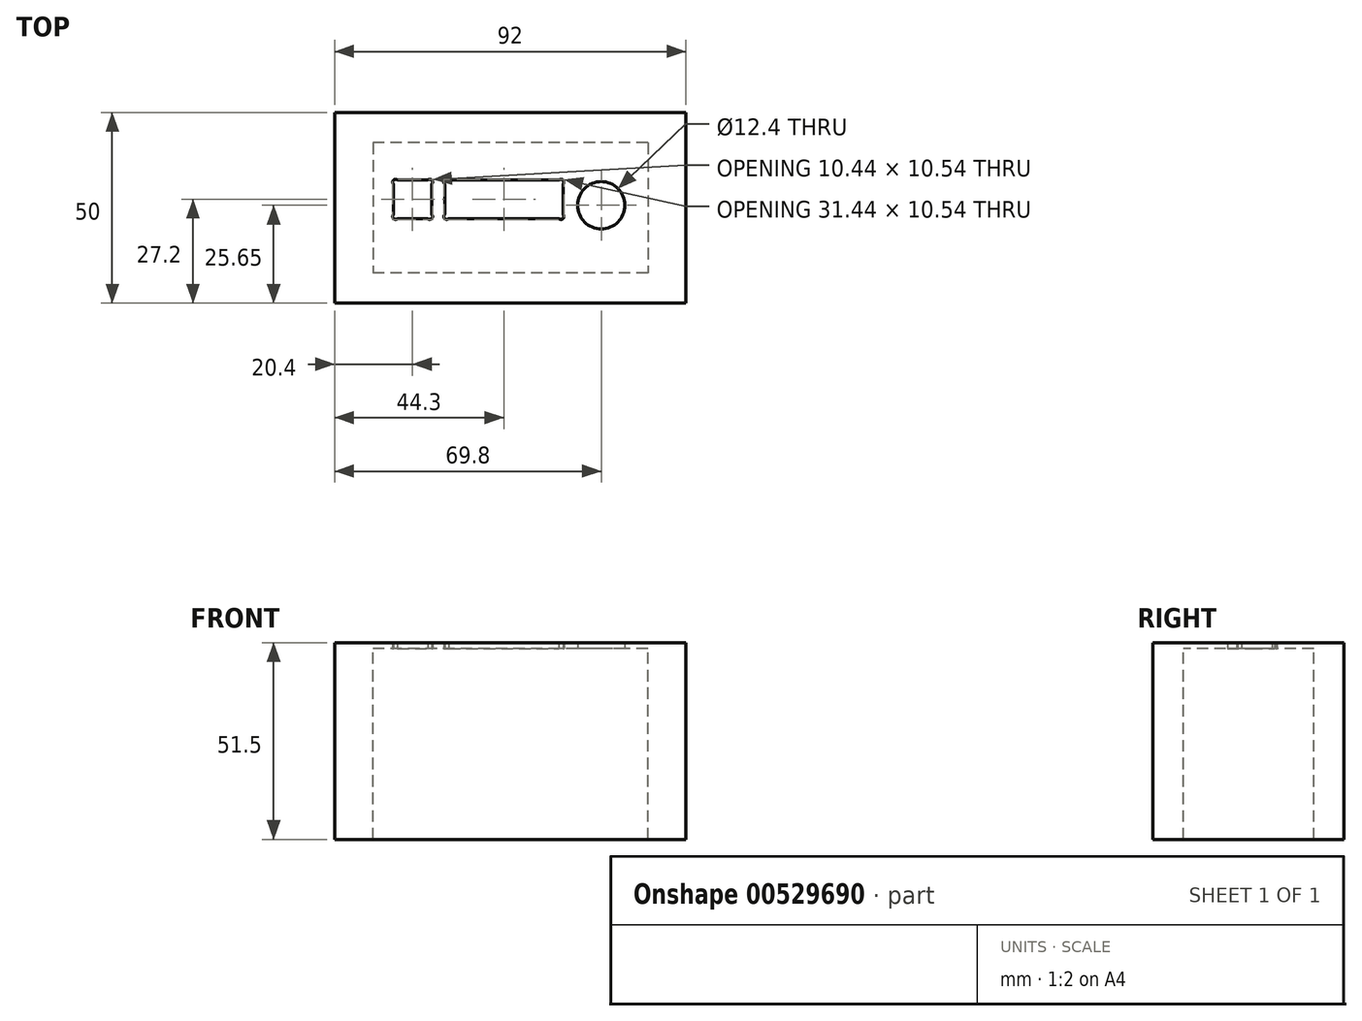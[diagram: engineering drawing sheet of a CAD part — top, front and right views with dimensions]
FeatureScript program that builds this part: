
annotation { "Feature Type Name" : "Feature", "Feature Type Description" : "" }
export const myFeature = defineFeature(function(context is Context, id is Id, definition is map)
    precondition{}
    {
        {
            var Q0;
            Q0=qCreatedBy(makeId("Top.planeOp"),FACE);
            var sketch = newSketch(context, id + "F0", { "sketchPlane" : qUnion([Q0])});
            skLineSegment(sketch, "E0.bottom", {"start": v(36, 17.05) * mm, "end": v(-36, 17.05) * mm});
            skLineSegment(sketch, "E0.top", {"start": v(36, -17.05) * mm, "end": v(-36, -17.05) * mm});
            skLineSegment(sketch, "E0.left", {"start": v(36, 17.05) * mm, "end": v(36, -17.05) * mm});
            skLineSegment(sketch, "E0.right", {"start": v(-36, 17.05) * mm, "end": v(-36, -17.05) * mm});
            skPoint(sketch, "E0.middle", {"position": v(0, 0) * mm});
            skLineSegment(sketch, "E1.bottom", {"start": v(46, 25) * mm, "end": v(-46, 25) * mm});
            skLineSegment(sketch, "E1.top", {"start": v(46, -25) * mm, "end": v(-46, -25) * mm});
            skLineSegment(sketch, "E1.left", {"start": v(46, 25) * mm, "end": v(46, -25) * mm});
            skLineSegment(sketch, "E1.right", {"start": v(-46, 25) * mm, "end": v(-46, -25) * mm});
            skLineSegment(sketch, "E2.bottom", {"start": v(-17.2, 7.25) * mm, "end": v(13.8, 7.25) * mm});
            skLineSegment(sketch, "E2.top", {"start": v(-17.2, -2.85) * mm, "end": v(13.8, -2.85) * mm});
            skLineSegment(sketch, "E2.left", {"start": v(-17.2, 7.25) * mm, "end": v(-17.2, -2.85) * mm});
            skLineSegment(sketch, "E2.right", {"start": v(13.8, 7.25) * mm, "end": v(13.8, -2.85) * mm});
            skLineSegment(sketch, "E3.bottom", {"start": v(-30.6, 7.25) * mm, "end": v(-20.6, 7.25) * mm});
            skLineSegment(sketch, "E3.top", {"start": v(-30.6, -2.85) * mm, "end": v(-20.6, -2.85) * mm});
            skLineSegment(sketch, "E3.left", {"start": v(-30.6, 7.25) * mm, "end": v(-30.6, -2.85) * mm});
            skLineSegment(sketch, "E3.right", {"start": v(-20.6, 7.25) * mm, "end": v(-20.6, -2.85) * mm});
            skCircle(sketch, "E4", {"center": v(23.8, 0.65) * mm, "radius": 6.2 * mm});
            skLineSegment(sketch, "E5", {"start": v(-30.6, 7.25) * mm, "end": v(-30.07, 6.72) * mm, "construction": true});
            skCircle(sketch, "E6", {"center": v(-30.07, 6.72) * mm, "radius": 0.75 * mm});
            skLineSegment(sketch, "E7", {"start": v(-20.6, 7.25) * mm, "end": v(-21.13, 6.72) * mm, "construction": true});
            skLineSegment(sketch, "E8", {"start": v(-20.6, -2.85) * mm, "end": v(-21.13, -2.32) * mm, "construction": true});
            skLineSegment(sketch, "E9", {"start": v(-30.6, -2.85) * mm, "end": v(-30.07, -2.32) * mm, "construction": true});
            skCircle(sketch, "E10", {"center": v(-30.07, -2.32) * mm, "radius": 0.75 * mm});
            skCircle(sketch, "E11", {"center": v(-21.13, -2.32) * mm, "radius": 0.75 * mm});
            skCircle(sketch, "E12", {"center": v(-21.13, 6.72) * mm, "radius": 0.75 * mm});
            skLineSegment(sketch, "E13", {"start": v(-17.2, 7.25) * mm, "end": v(-16.67, 6.72) * mm, "construction": true});
            skLineSegment(sketch, "E14", {"start": v(-17.2, -2.85) * mm, "end": v(-16.67, -2.32) * mm, "construction": true});
            skLineSegment(sketch, "E15", {"start": v(13.8, -2.85) * mm, "end": v(13.27, -2.32) * mm, "construction": true});
            skLineSegment(sketch, "E16", {"start": v(13.8, 7.25) * mm, "end": v(13.27, 6.72) * mm, "construction": true});
            skCircle(sketch, "E17", {"center": v(13.27, 6.72) * mm, "radius": 0.75 * mm});
            skCircle(sketch, "E18", {"center": v(13.27, -2.32) * mm, "radius": 0.75 * mm});
            skCircle(sketch, "E19", {"center": v(-16.67, -2.32) * mm, "radius": 0.75 * mm});
            skCircle(sketch, "E20", {"center": v(-16.67, 6.72) * mm, "radius": 0.75 * mm});
            skSolve(sketch);
        }
        {
            var Q0;
            Q0=makeQuery(id+"F0.imprint","IMPRINT",FACE,{"disambiguationData":[TD([[makeQuery(id+"F0.imprint","IMPRINT",EDGE,{"derivedFrom":sQuery(id+"F0.wireOp",EDGE,"E0.bottom")}),-1.0]])]});
            extrude(context, id + "F1", {"entities" : qUnion([Q0]), "oppositeDirection" : true, "depth" : 50 * mm, "offsetDistance" : 25 * mm});
        }
        {
            var Q0;
            Q0=makeQuery(id+"F0.imprint","IMPRINT",FACE,{"disambiguationData":[TD([[makeQuery(id+"F0.imprint","IMPRINT",EDGE,{"derivedFrom":sQuery(id+"F0.wireOp",EDGE,"E0.bottom")}),-1.0]])]});
            var Q1;
            Q1=makeQuery(id+"F0.imprint","IMPRINT",FACE,{"disambiguationData":[TD([[makeQuery(id+"F0.imprint","IMPRINT",EDGE,{"derivedFrom":sQuery(id+"F0.wireOp",EDGE,"E0.bottom")}),1.0]])]});
            extrude(context, id + "F2", {"entities" : qUnion([Q0, Q1]), "operationType" : NewBodyOperationType.ADD, "depth" : 1.5 * mm, "offsetDistance" : 25 * mm});
        }
    });
